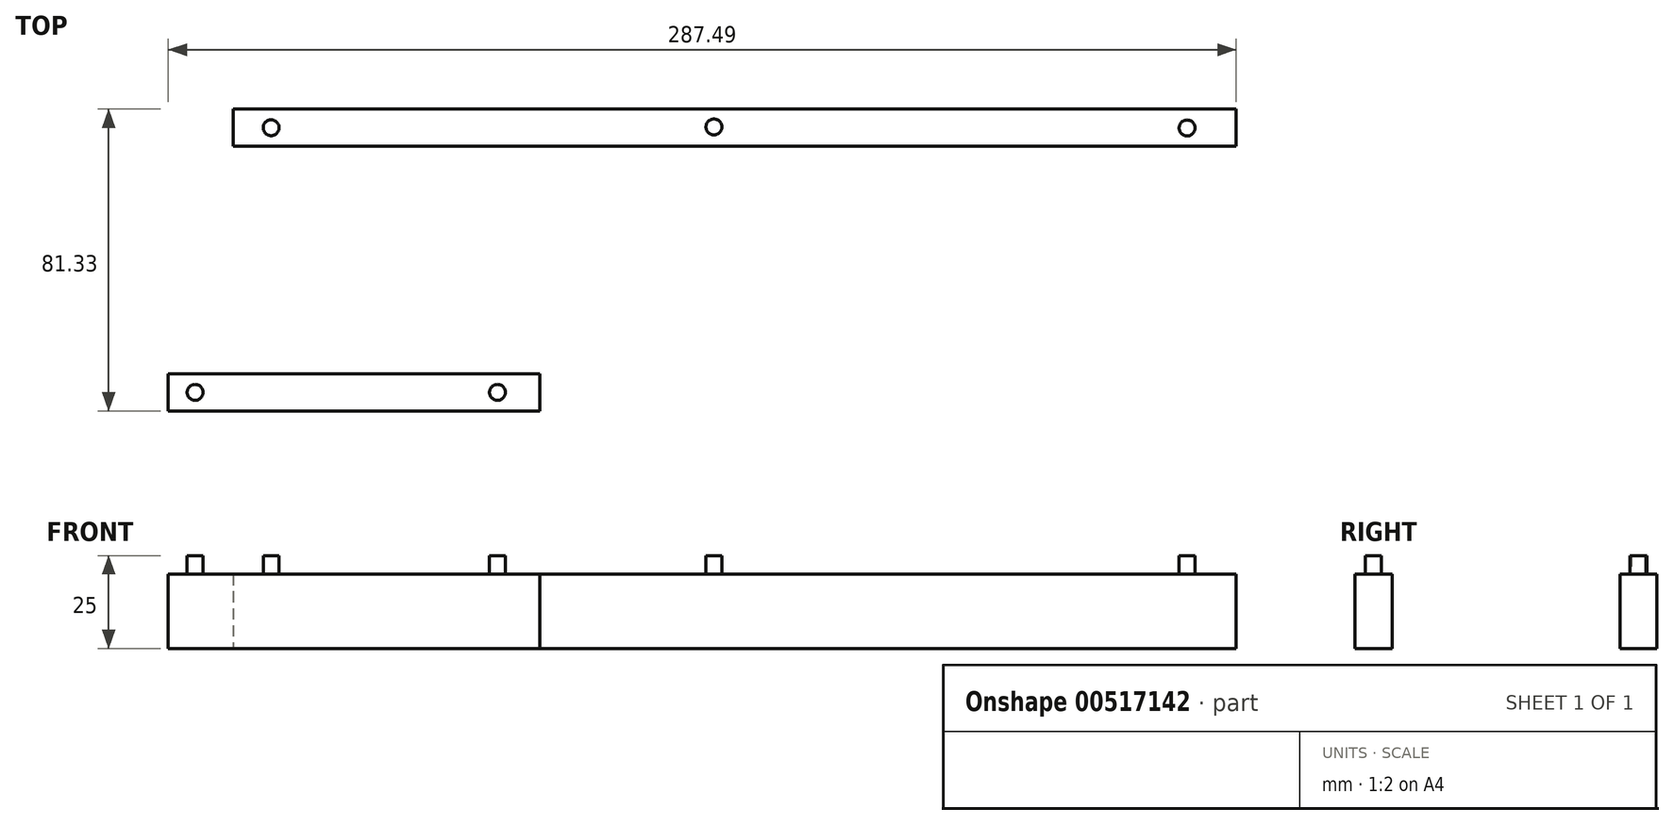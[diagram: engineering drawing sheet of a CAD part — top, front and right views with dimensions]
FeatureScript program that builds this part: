
annotation { "Feature Type Name" : "Feature", "Feature Type Description" : "" }
export const myFeature = defineFeature(function(context is Context, id is Id, definition is map)
    precondition{}
    {
        {
            var Q0;
            Q0=qCreatedBy(makeId("Top.planeOp"),FACE);
            var sketch = newSketch(context, id + "F0", { "sketchPlane" : qUnion([Q0])});
            skLineSegment(sketch, "E0", {"start": v(-72.62, -18.76) * mm, "end": v(-72.62, -28.76) * mm});
            skLineSegment(sketch, "E1", {"start": v(-72.62, -28.76) * mm, "end": v(27.38, -28.76) * mm});
            skLineSegment(sketch, "E2", {"start": v(27.38, -28.76) * mm, "end": v(27.38, -18.76) * mm});
            skLineSegment(sketch, "E3", {"start": v(27.38, -18.76) * mm, "end": v(-72.62, -18.76) * mm});
            skSolve(sketch);
        }
        {
            var Q0;
            Q0=makeQuery(id+"F0.imprint","IMPRINT",FACE,{"disambiguationData":[TD([[makeQuery(id+"F0.imprint","IMPRINT",EDGE,{"derivedFrom":sQuery(id+"F0.wireOp",EDGE,"E0")}),1.0]])]});
            extrude(context, id + "F1", {"entities" : qUnion([Q0]), "depth" : 20 * mm, "offsetDistance" : 25 * mm});
        }
        {
            var Q0;
            Q0=qCreatedBy(makeId("Top.planeOp"),FACE);
            var sketch = newSketch(context, id + "F2", { "sketchPlane" : qUnion([Q0])});
            skLineSegment(sketch, "E4.bottom", {"start": v(-21.66, 53.5) * mm, "end": v(48.34, 53.5) * mm});
            skLineSegment(sketch, "E4.top", {"start": v(-21.66, 43.5) * mm, "end": v(48.34, 43.5) * mm});
            skLineSegment(sketch, "E4.left", {"start": v(-21.66, 53.5) * mm, "end": v(-21.66, 43.5) * mm});
            skLineSegment(sketch, "E4.right", {"start": v(48.34, 53.5) * mm, "end": v(48.34, 43.5) * mm});
            skSolve(sketch);
        }
        {
            var Q0;
            Q0=makeQuery(id+"F2.imprint","IMPRINT",FACE,{"disambiguationData":[TD([[makeQuery(id+"F2.imprint","IMPRINT",EDGE,{"derivedFrom":sQuery(id+"F2.wireOp",EDGE,"E4.bottom")}),-1.0]])]});
            extrude(context, id + "F3", {"entities" : qUnion([Q0]), "depth" : 30 * mm, "offsetDistance" : 25 * mm});
        }
        {
            var Q0;
            Q0=makeQuery(id+"F3.opExtrude","SWEPT_BODY",BODY,{"disambiguationData":[OSD([sQuery(id+"F2.wireOp",EDGE,"E4.bottom"),sQuery(id+"F2.wireOp",EDGE,"E4.top"),sQuery(id+"F2.wireOp",EDGE,"E4.left"),sQuery(id+"F2.wireOp",EDGE,"E4.right")])]});
            deleteBodies(context, id + "F4", {"entities" : qUnion([Q0])});
        }
        {
            var Q0;
            Q0=qCreatedBy(makeId("Top.planeOp"),FACE);
            var sketch = newSketch(context, id + "F5", { "sketchPlane" : qUnion([Q0])});
            skLineSegment(sketch, "E5.bottom", {"start": v(-55.13, 52.57) * mm, "end": v(214.87, 52.57) * mm});
            skLineSegment(sketch, "E5.top", {"start": v(-55.13, 42.57) * mm, "end": v(214.87, 42.57) * mm});
            skLineSegment(sketch, "E5.left", {"start": v(-55.13, 52.57) * mm, "end": v(-55.13, 42.57) * mm});
            skLineSegment(sketch, "E5.right", {"start": v(214.87, 52.57) * mm, "end": v(214.87, 42.57) * mm});
            skSolve(sketch);
        }
        {
            var Q0;
            Q0 = qSketchRegion(id + "F5", true);
            extrude(context, id + "F6", {"entities" : qUnion([Q0]), "depth" : 20 * mm, "offsetDistance" : 25 * mm});
        }
        {
            var Q0;
            Q0=makeQuery(id+"F6.opExtrude","CAP_FACE",FACE,{"disambiguationData":[OSD([sQuery(id+"F5.wireOp",EDGE,"E5.bottom"),sQuery(id+"F5.wireOp",EDGE,"E5.top"),sQuery(id+"F5.wireOp",EDGE,"E5.left"),sQuery(id+"F5.wireOp",EDGE,"E5.right")])],"isStart":false});
            var sketch = newSketch(context, id + "F7", { "sketchPlane" : qUnion([Q0])});
            skCircle(sketch, "E6", {"center": v(-44.9, 47.57) * mm, "radius": 2.15 * mm});
            skPoint(sketch, "E6.centerSnap0", {"position": v(-55.13, 47.57) * mm});
            skCircle(sketch, "E7", {"center": v(74.3, 47.77) * mm, "radius": 2.15 * mm});
            skCircle(sketch, "E8", {"center": v(201.69, 47.49) * mm, "radius": 2.15 * mm});
            skSolve(sketch);
        }
        {
            var Q0;
            Q0 = qSketchRegion(id + "F7", true);
            extrude(context, id + "F8", {"entities" : qUnion([Q0]), "operationType" : NewBodyOperationType.ADD, "depth" : 5 * mm, "offsetDistance" : 25 * mm});
        }
        {
            var Q0;
            Q0=makeQuery(id+"F1.opExtrude","CAP_FACE",FACE,{"disambiguationData":[OSD([sQuery(id+"F0.wireOp",EDGE,"E0"),sQuery(id+"F0.wireOp",EDGE,"E1"),sQuery(id+"F0.wireOp",EDGE,"E2"),sQuery(id+"F0.wireOp",EDGE,"E3")])],"isStart":false});
            var sketch = newSketch(context, id + "F9", { "sketchPlane" : qUnion([Q0])});
            skCircle(sketch, "E9", {"center": v(-65.37, -23.76) * mm, "radius": 2.15 * mm});
            skPoint(sketch, "E9.centerSnap0", {"position": v(-72.62, -23.76) * mm});
            skCircle(sketch, "E10", {"center": v(16.04, -23.76) * mm, "radius": 2.15 * mm});
            skPoint(sketch, "E10.centerSnap0", {"position": v(27.38, -23.76) * mm});
            skSolve(sketch);
        }
        {
            var Q0;
            Q0 = qSketchRegion(id + "F9", true);
            extrude(context, id + "F10", {"entities" : qUnion([Q0]), "operationType" : NewBodyOperationType.ADD, "depth" : 5 * mm, "offsetDistance" : 25 * mm});
        }
        {
            var Q0;
            Q0=makeQuery(id+"F1.opExtrude","SWEPT_BODY",BODY,{"disambiguationData":[OSD([sQuery(id+"F0.wireOp",EDGE,"E0"),sQuery(id+"F0.wireOp",EDGE,"E1"),sQuery(id+"F0.wireOp",EDGE,"E2"),sQuery(id+"F0.wireOp",EDGE,"E3")])]});
            transform(context, id + "F11", {"entities" : qUnion([Q0]), "transformType" : TransformType.TRANSLATION_3D, "dx" : 0 * mm, "dy" : 0 * mm, "dz" : 0 * mm, "makeCopy" : true});
        }
    });
